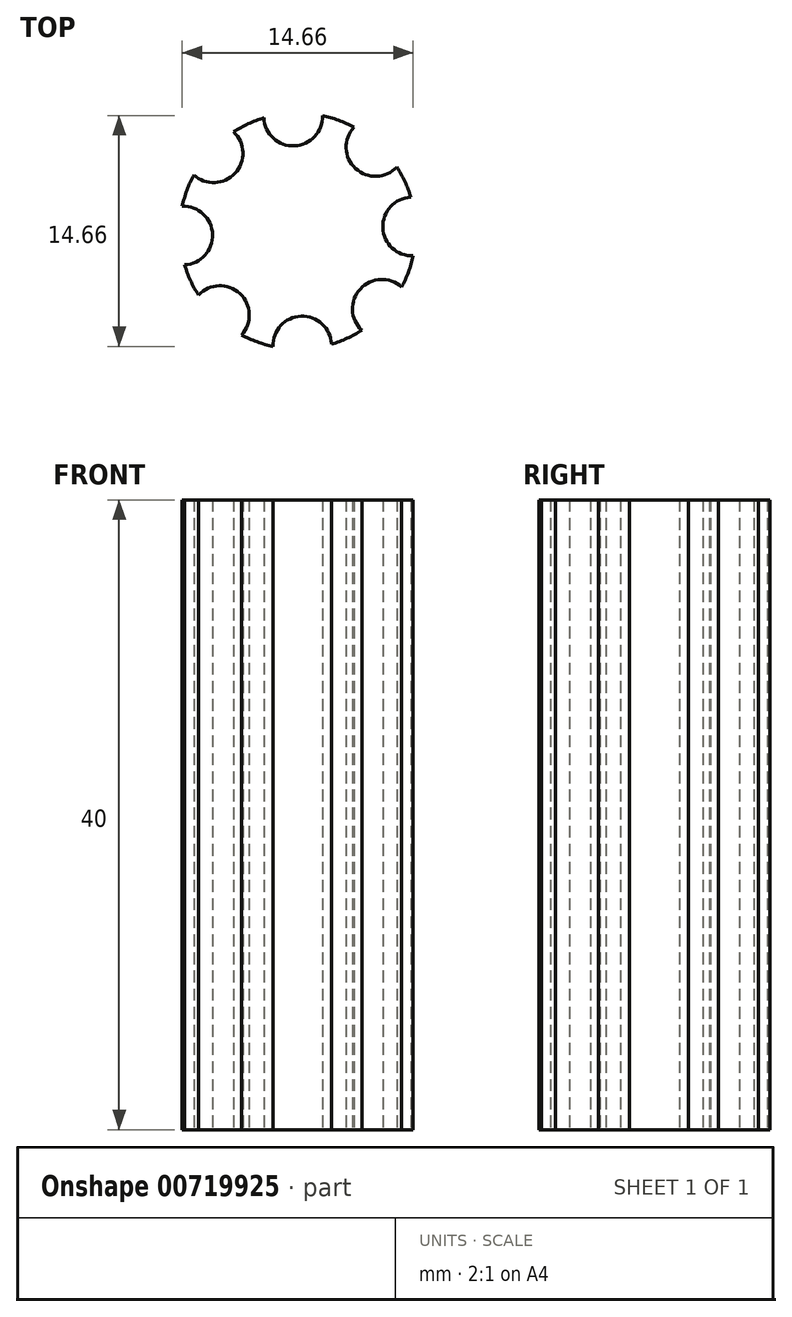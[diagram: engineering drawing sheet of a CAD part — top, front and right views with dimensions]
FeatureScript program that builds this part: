
annotation { "Feature Type Name" : "Feature", "Feature Type Description" : "" }
export const myFeature = defineFeature(function(context is Context, id is Id, definition is map)
    precondition{}
    {
        {
            var Q0;
            Q0=qCreatedBy(makeId("Top.planeOp"),FACE);
            var sketch = newSketch(context, id + "F0", { "sketchPlane" : qUnion([Q0])});
            skCircle(sketch, "E0", {"center": v(0, 0) * mm, "radius": 7.5 * mm});
            skArc(sketch, "E1", {"start": v(-6.6, 3.56) * mm, "mid": v(-3.97, 3.67) * mm, "end": v(-4.07, 6.3) * mm});
            skArc(sketch, "E2.1.0", {"start": v(-7.19, -2.15) * mm, "mid": v(-5.4, -0.21) * mm, "end": v(-7.33, 1.58) * mm});
            skArc(sketch, "E2.2.0", {"start": v(-3.56, -6.6) * mm, "mid": v(-3.67, -3.97) * mm, "end": v(-6.3, -4.07) * mm});
            skArc(sketch, "E2.3.0", {"start": v(2.15, -7.19) * mm, "mid": v(0.21, -5.4) * mm, "end": v(-1.58, -7.33) * mm});
            skArc(sketch, "E2.4.0", {"start": v(6.6, -3.56) * mm, "mid": v(3.97, -3.67) * mm, "end": v(4.07, -6.3) * mm});
            skArc(sketch, "E2.5.0", {"start": v(7.19, 2.15) * mm, "mid": v(5.4, 0.21) * mm, "end": v(7.33, -1.58) * mm});
            skArc(sketch, "E2.6.0", {"start": v(3.56, 6.6) * mm, "mid": v(3.67, 3.97) * mm, "end": v(6.3, 4.07) * mm});
            skArc(sketch, "E2.7.0", {"start": v(-2.15, 7.19) * mm, "mid": v(-0.21, 5.4) * mm, "end": v(1.58, 7.33) * mm});
            skSolve(sketch);
        }
        {
            var Q0;
            Q0=makeQuery(id+"F0.imprint","IMPRINT",FACE,{"disambiguationData":[TD([[makeQuery(id+"F0.imprint","IMPRINT",EDGE,{"derivedFrom":sQuery(id+"F0.wireOp",EDGE,"E0")}),1.0]])]});
            extrude(context, id + "F1", {"entities" : qUnion([Q0]), "depth" : 40 * mm, "offsetDistance" : 25 * mm});
        }
    });
